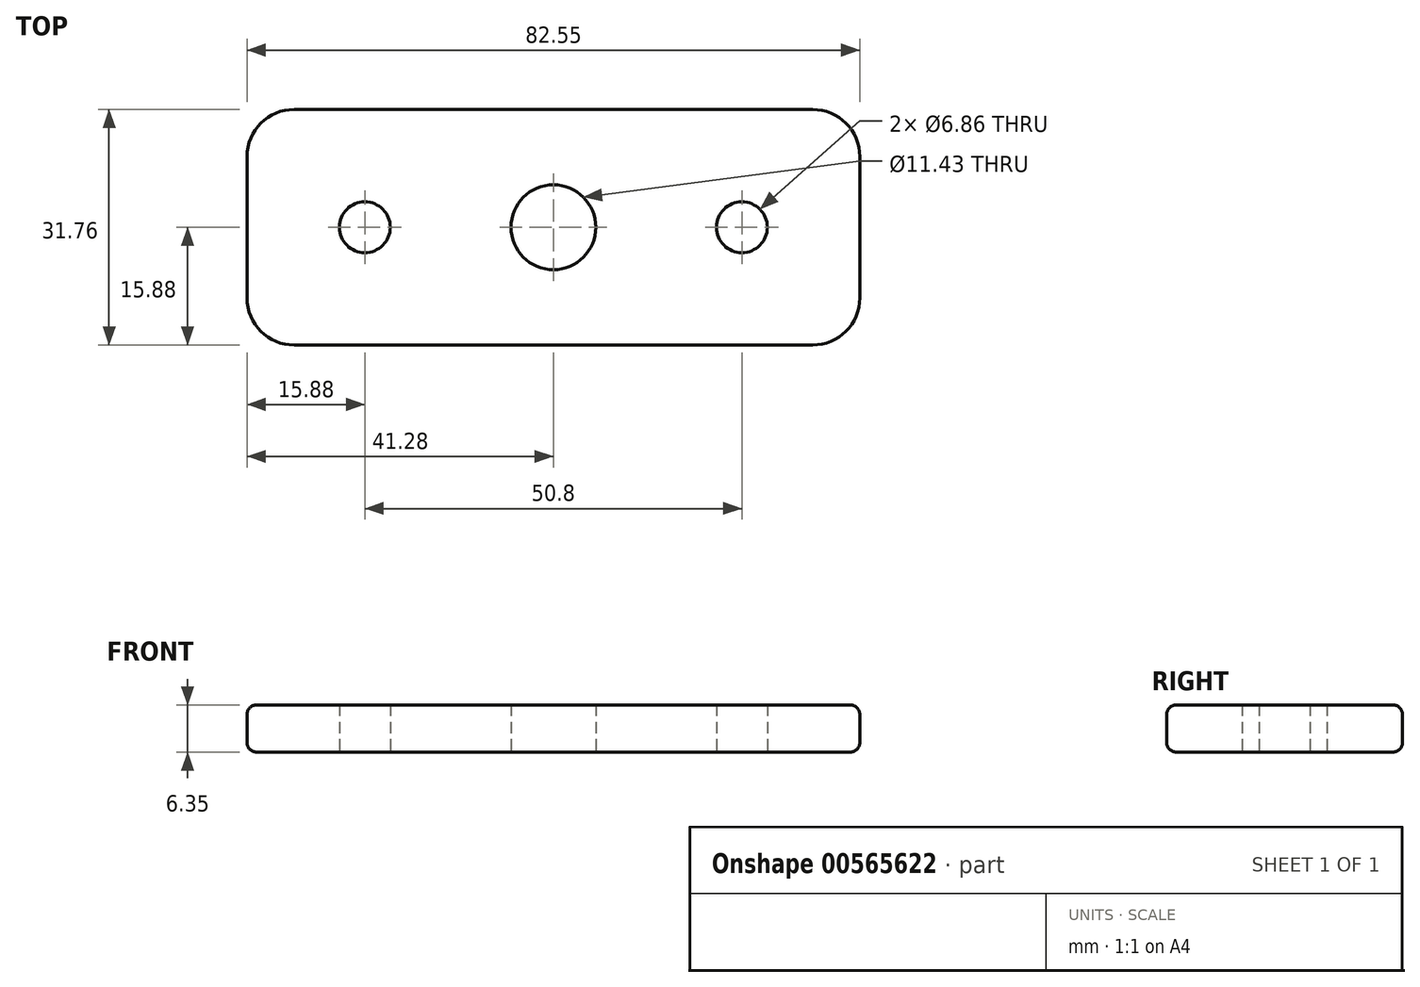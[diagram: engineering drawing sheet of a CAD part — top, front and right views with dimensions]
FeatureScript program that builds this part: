
annotation { "Feature Type Name" : "Feature", "Feature Type Description" : "" }
export const myFeature = defineFeature(function(context is Context, id is Id, definition is map)
    precondition{}
    {
        {
            var Q0;
            Q0=qCreatedBy(makeId("Top.planeOp"),FACE);
            var sketch = newSketch(context, id + "F0", { "sketchPlane" : qUnion([Q0])});
            skLineSegment(sketch, "E0.bottom", {"start": v(41.28, 15.88) * mm, "end": v(-41.27, 15.88) * mm});
            skLineSegment(sketch, "E0.top", {"start": v(41.27, -15.88) * mm, "end": v(-41.28, -15.88) * mm});
            skLineSegment(sketch, "E0.left", {"start": v(41.28, 15.88) * mm, "end": v(41.27, -15.88) * mm});
            skLineSegment(sketch, "E0.right", {"start": v(-41.27, 15.88) * mm, "end": v(-41.28, -15.88) * mm});
            skPoint(sketch, "E0.middle", {"position": v(0, 0) * mm});
            skCircle(sketch, "E1", {"center": v(0, 0) * mm, "radius": 5.72 * mm});
            skCircle(sketch, "E2", {"center": v(25.4, 0) * mm, "radius": 3.43 * mm});
            skCircle(sketch, "E3.MirrorC", {"center": v(-25.4, 0) * mm, "radius": 3.43 * mm});
            skSolve(sketch);
        }
        {
            var Q0;
            Q0=makeQuery(id+"F0.imprint","IMPRINT",FACE,{"disambiguationData":[TD([[makeQuery(id+"F0.imprint","IMPRINT",EDGE,{"derivedFrom":sQuery(id+"F0.wireOp",EDGE,"E0.bottom")}),1.0]])]});
            extrude(context, id + "F1", {"entities" : qUnion([Q0]), "depth" : 6.35 * mm, "offsetDistance" : 25.4 * mm});
        }
        {
            var Q0;
            Q0=makeQuery(id+"F1.opExtrude","SWEPT_EDGE",EDGE,{"disambiguationData":[OSD([sQuery(id+"F0.wireOp",EDGE,"E0.top"),sQuery(id+"F0.wireOp",EDGE,"E0.right")])]});
            var Q1;
            Q1=makeQuery(id+"F1.opExtrude","SWEPT_EDGE",EDGE,{"disambiguationData":[OSD([sQuery(id+"F0.wireOp",EDGE,"E0.top"),sQuery(id+"F0.wireOp",EDGE,"E0.left")])]});
            var Q2;
            Q2=makeQuery(id+"F1.opExtrude","SWEPT_EDGE",EDGE,{"disambiguationData":[OSD([sQuery(id+"F0.wireOp",EDGE,"E0.bottom"),sQuery(id+"F0.wireOp",EDGE,"E0.left")])]});
            var Q3;
            Q3=makeQuery(id+"F1.opExtrude","SWEPT_EDGE",EDGE,{"disambiguationData":[OSD([sQuery(id+"F0.wireOp",EDGE,"E0.bottom"),sQuery(id+"F0.wireOp",EDGE,"E0.right")])]});
            fillet(context, id + "F2", {"entities" : qUnion([Q0, Q1, Q2, Q3]), "radius" : 6.35 * mm, "tangentPropagation" : true, "allowEdgeOverflow" : false});
        }
        {
            var Q0;
            Q0=makeQuery(id+"F1.opExtrude","CAP_EDGE",EDGE,{"disambiguationData":[OSD([sQuery(id+"F0.wireOp",EDGE,"E0.top")])],"isStart":false});
            var Q1;
            Q1=makeQuery(id+"F1.opExtrude","CAP_EDGE",EDGE,{"disambiguationData":[OSD([sQuery(id+"F0.wireOp",EDGE,"E0.top")])],"isStart":true});
            fillet(context, id + "F3", {"entities" : qUnion([Q0, Q1]), "radius" : 1.27 * mm, "tangentPropagation" : true, "allowEdgeOverflow" : false});
        }
    });
